# Revit family: FireFighting_Hydrant-Pipe-Riser-Dual-Head_Galvin_100x1500
name_source: partatom
category: Mechanical Equipment
revit_build: Autodesk Revit MEP 2012 (Build: 20110916_2132(x64)
units: mm (PartAtom-declared; Revit-internal decimal feet)

## types (2) — shared parameters
Assembly Code = D4030
Description = Hydrant Pipe Riser with Dual Head, Flanged Vertical Inlet 100 X 1500 Long (Galvanized & Painted)
DimHeight = 960 mm  [stored 3.14961 ft]
DimInletRadius = 50 mm  [stored 0.164042 ft]
FilterObject_ANZRS = 381337
FlowRate = 0.00 L/s
Instructions = http://www.galvinengineering.com.au
Keynote = 10520
Manufacturer = Galvin Engineering
Model = 381337
ModifiedIssue_ANZRS = 20140330 $
StyleOrType_ANZRS = Fire Fighting Equipment
Type Comments = 381337
URL = www.galvinengineering.com.au

## per-type parameters (varying)
| type | Valves |
| 381337 | No |
| 381337 With Valves | Yes |

note: [stored X ft] marks values corroborated as IEEE doubles in the binary element streams (Revit-internal decimal feet)

## geometry (parser evidence)
native form markers: Blend x2, Sweep x1
no freeform markers — native parametric forms only
